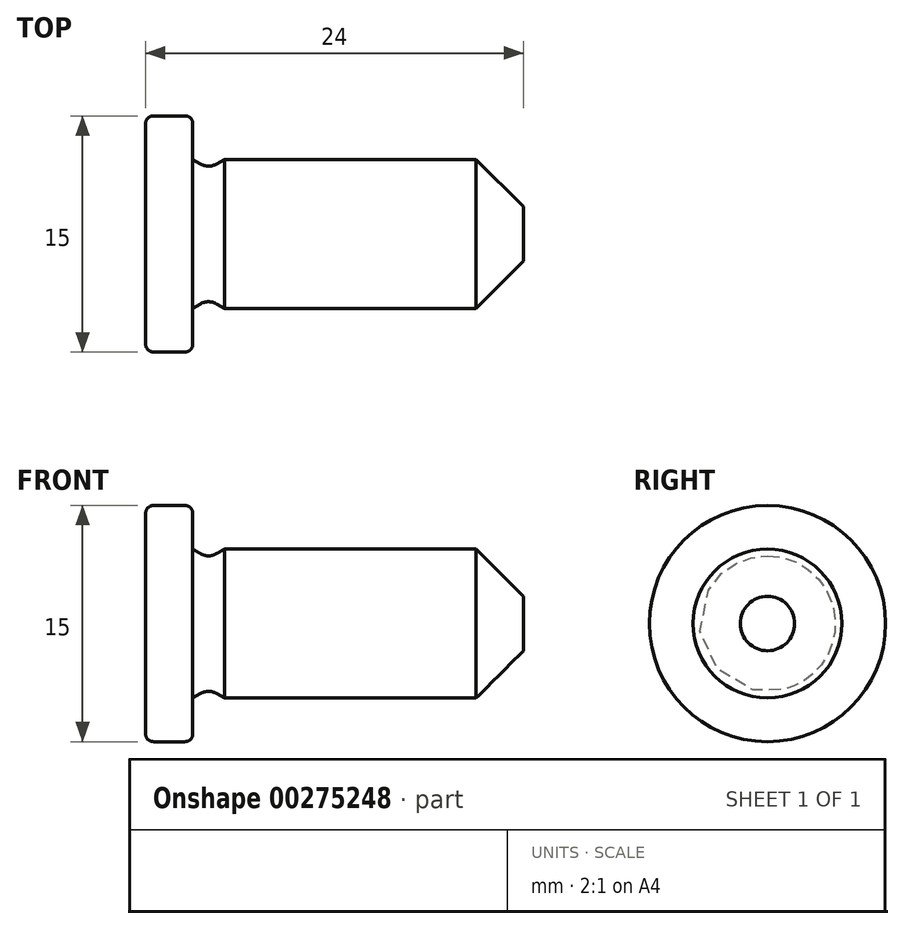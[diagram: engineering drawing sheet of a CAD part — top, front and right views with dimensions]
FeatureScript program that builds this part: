
annotation { "Feature Type Name" : "Feature", "Feature Type Description" : "" }
export const myFeature = defineFeature(function(context is Context, id is Id, definition is map)
    precondition{}
    {
        {
            var Q0;
            Q0=qCreatedBy(makeId("Front.planeOp"),FACE);
            var sketch = newSketch(context, id + "F0", { "sketchPlane" : qUnion([Q0])});
            skLineSegment(sketch, "E0", {"start": v(0, 0) * mm, "end": v(0, 7.5) * mm});
            skLineSegment(sketch, "E1", {"start": v(0, 7.5) * mm, "end": v(3, 7.5) * mm});
            skLineSegment(sketch, "E2", {"start": v(3, 7.5) * mm, "end": v(3, 0) * mm});
            skLineSegment(sketch, "E3", {"start": v(3, 0) * mm, "end": v(0, 0) * mm});
            skLineSegment(sketch, "E4", {"start": v(4, 0) * mm, "end": v(4, 4.15) * mm});
            skLineSegment(sketch, "E5", {"start": v(5, 4.73) * mm, "end": v(5, 0) * mm});
            skLineSegment(sketch, "E6", {"start": v(4, 4.15) * mm, "end": v(5, 4.73) * mm});
            skLineSegment(sketch, "E7", {"start": v(4, 4.15) * mm, "end": v(3, 4.73) * mm});
            skLineSegment(sketch, "E8", {"start": v(5, 4.73) * mm, "end": v(24, 4.73) * mm});
            skLineSegment(sketch, "E9", {"start": v(24, 4.73) * mm, "end": v(24, 0) * mm});
            skLineSegment(sketch, "E10", {"start": v(0, 0) * mm, "end": v(24, 0) * mm});
            skSolve(sketch);
        }
        {
            var Q0;
            Q0 = qSketchRegion(id + "F0", true);
            var Q1;
            Q1=sQuery(id+"F0.wireOp",EDGE,"E10");
            revolve(context, id + "F1", {"entities" : qUnion([Q0]), "axis" : qUnion([Q1]), "revolveType" : RevolveType.FULL});
        }
        {
            var Q0;
            Q0=makeQuery(id+"F1.opRevolve","SWEPT_EDGE",EDGE,{"disambiguationData":[OSD([sQuery(id+"F0.wireOp",EDGE,"E4"),sQuery(id+"F0.wireOp",EDGE,"E6"),sQuery(id+"F0.wireOp",EDGE,"E7")])]});
            fillet(context, id + "F2", {"entities" : qUnion([Q0]), "radius" : 1 * mm, "tangentPropagation" : true, "allowEdgeOverflow" : false});
        }
        {
            var Q0;
            Q0=makeQuery(id+"F1.opRevolve","SWEPT_EDGE",EDGE,{"disambiguationData":[OSD([sQuery(id+"F0.wireOp",EDGE,"E0"),sQuery(id+"F0.wireOp",EDGE,"E1")])]});
            var Q1;
            Q1=makeQuery(id+"F1.opRevolve","SWEPT_EDGE",EDGE,{"disambiguationData":[OSD([sQuery(id+"F0.wireOp",EDGE,"E1"),sQuery(id+"F0.wireOp",EDGE,"E2")])]});
            fillet(context, id + "F3", {"entities" : qUnion([Q0, Q1]), "radius" : .5 * mm, "tangentPropagation" : true, "allowEdgeOverflow" : false});
        }
        {
            var Q0;
            Q0=makeQuery(id+"F1.opRevolve","SWEPT_EDGE",EDGE,{"disambiguationData":[OSD([sQuery(id+"F0.wireOp",EDGE,"E8"),sQuery(id+"F0.wireOp",EDGE,"E9")])]});
            chamfer(context, id + "F4", {"entities" : qUnion([Q0]), "chamferType" : ChamferType.OFFSET_ANGLE, "width" : 3 * mm, "oppositeDirection" : false, "angle" : 45 * degree, "tangentPropagation" : true});
        }
    });
